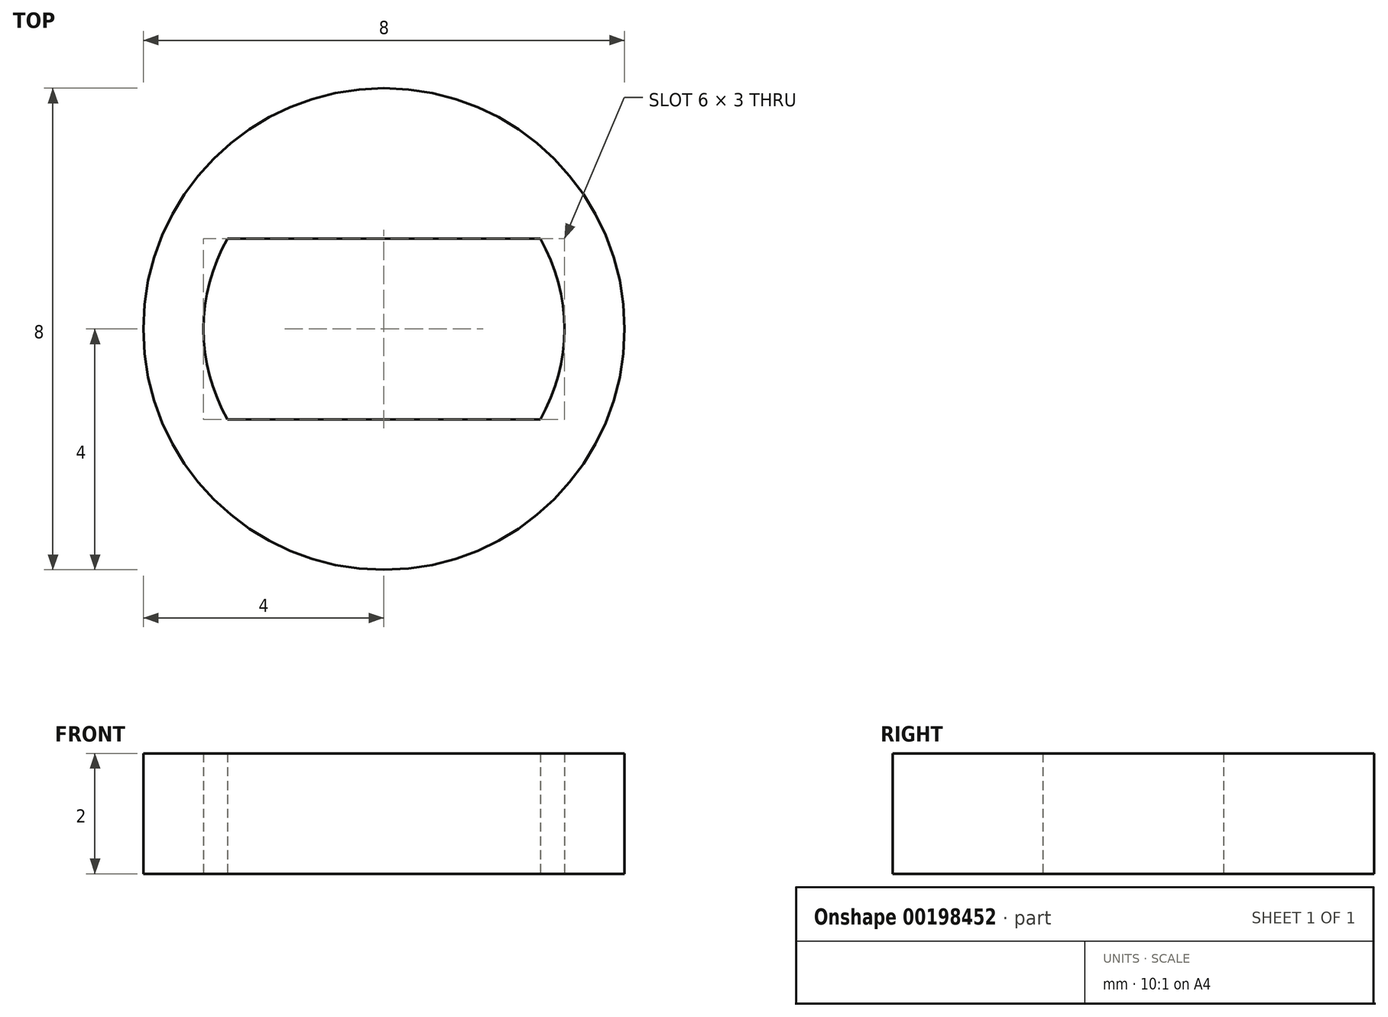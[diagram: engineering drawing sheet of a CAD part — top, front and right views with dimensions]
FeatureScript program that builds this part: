
annotation { "Feature Type Name" : "Feature", "Feature Type Description" : "" }
export const myFeature = defineFeature(function(context is Context, id is Id, definition is map)
    precondition{}
    {
        {
            var Q0;
            Q0=qCreatedBy(makeId("Top.planeOp"),FACE);
            var sketch = newSketch(context, id + "F0", { "sketchPlane" : qUnion([Q0])});
            skCircle(sketch, "E0", {"center": v(0, 0) * mm, "radius": 4 * mm});
            skArc(sketch, "E1", {"start": v(-2.6, 1.5) * mm, "mid": v(-3, 0) * mm, "end": v(-2.6, -1.5) * mm});
            skLineSegment(sketch, "E2.bottom", {"start": v(2.6, 1.5) * mm, "end": v(-2.6, 1.5) * mm});
            skLineSegment(sketch, "E2.top", {"start": v(2.6, -1.5) * mm, "end": v(-2.6, -1.5) * mm});
            skPoint(sketch, "E3.orphan", {"position": v(-3.35, 1.5) * mm});
            skPoint(sketch, "E2.left.start.orphan", {"position": v(3.35, 1.5) * mm});
            skPoint(sketch, "E4.orphan", {"position": v(3.35, -1.5) * mm});
            skArc(sketch, "E5.trimOffspring", {"start": v(2.6, -1.5) * mm, "mid": v(3, 0) * mm, "end": v(2.6, 1.5) * mm});
            skPoint(sketch, "E6.orphan", {"position": v(-3.35, -1.5) * mm});
            skSolve(sketch);
        }
        {
            var Q0;
            Q0 = qSketchRegion(id + "F0", true);
            extrude(context, id + "F1", {"entities" : qUnion([Q0]), "depth" : 2 * mm});
        }
    });
